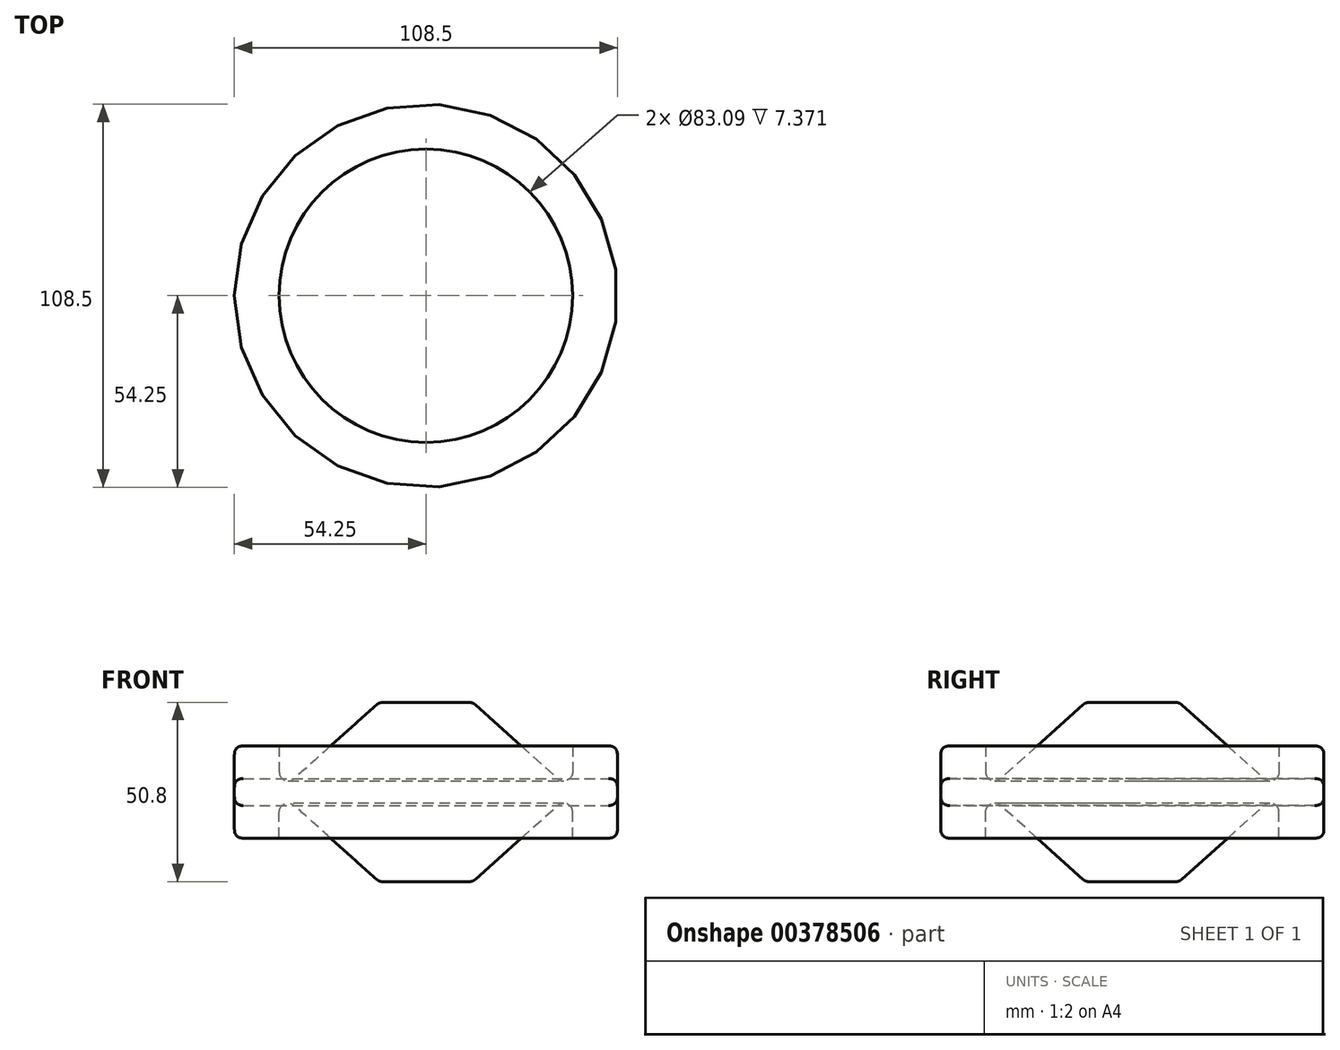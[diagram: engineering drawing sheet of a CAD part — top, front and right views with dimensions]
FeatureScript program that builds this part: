
annotation { "Feature Type Name" : "Feature", "Feature Type Description" : "" }
export const myFeature = defineFeature(function(context is Context, id is Id, definition is map)
    precondition{}
    {
        {
            var Q0;
            Q0=qCreatedBy(makeId("Front.planeOp"),FACE);
            var sketch = newSketch(context, id + "F0", { "sketchPlane" : qUnion([Q0])});
            skLineSegment(sketch, "E0", {"start": v(0, 0) * mm, "end": v(0, 25.4) * mm});
            skLineSegment(sketch, "E1", {"start": v(0, 25.4) * mm, "end": v(-13.24, 25.4) * mm});
            skLineSegment(sketch, "E2", {"start": v(-13.24, 25.4) * mm, "end": v(-41.55, 0) * mm});
            skLineSegment(sketch, "E3", {"start": v(-41.55, 0) * mm, "end": v(-41.55, 13.06) * mm});
            skLineSegment(sketch, "E4", {"start": v(-41.55, 13.06) * mm, "end": v(-54.25, 13.06) * mm});
            skLineSegment(sketch, "E5", {"start": v(-54.25, 13.06) * mm, "end": v(-54.25, 0) * mm});
            skLineSegment(sketch, "E6", {"start": v(-54.25, 0) * mm, "end": v(-54.25, -3.81) * mm});
            skLineSegment(sketch, "E7", {"start": v(-54.25, -3.81) * mm, "end": v(0, -3.81) * mm});
            skLineSegment(sketch, "E8", {"start": v(0, -3.81) * mm, "end": v(0, 0) * mm});
            skSolve(sketch);
        }
        {
            var Q0;
            Q0=makeQuery(id+"F0.imprint","IMPRINT",FACE,{"disambiguationData":[TD([[makeQuery(id+"F0.imprint","IMPRINT",EDGE,{"derivedFrom":sQuery(id+"F0.wireOp",EDGE,"E0")}),1.0]])]});
            var Q1;
            Q1=sQuery(id+"F0.wireOp",EDGE,"E0");
            revolve(context, id + "F1", {"entities" : qUnion([Q0]), "axis" : qUnion([Q1]), "revolveType" : RevolveType.FULL});
        }
        {
            var Q0;
            Q0=makeQuery(id+"F1.opRevolve","SWEPT_FACE",FACE,{"disambiguationData":[OSD([sQuery(id+"F0.wireOp",EDGE,"E2")])]});
            fillet(context, id + "F2", {"entities" : qUnion([Q0]), "radius" : 2.54 * mm, "tangentPropagation" : true, "allowEdgeOverflow" : false});
        }
        {
            var Q0;
            Q0=makeQuery(id+"F1.opRevolve","SWEPT_FACE",FACE,{"disambiguationData":[OSD([sQuery(id+"F0.wireOp",EDGE,"E5"),sQuery(id+"F0.wireOp",EDGE,"E6")])]});
            fillet(context, id + "F3", {"entities" : qUnion([Q0]), "radius" : 2.54 * mm, "tangentPropagation" : true, "rho" : 0.5, "crossSection" : FilletCrossSection.CONIC, "allowEdgeOverflow" : false});
        }
        {
            var Q0;
            Q0=makeQuery(id+"F1.opRevolve","SWEPT_BODY",BODY,{"disambiguationData":[OSD([sQuery(id+"F0.wireOp",EDGE,"E0"),sQuery(id+"F0.wireOp",EDGE,"E1"),sQuery(id+"F0.wireOp",EDGE,"E2"),sQuery(id+"F0.wireOp",EDGE,"E3"),sQuery(id+"F0.wireOp",EDGE,"E4"),sQuery(id+"F0.wireOp",EDGE,"E5"),sQuery(id+"F0.wireOp",EDGE,"E6"),sQuery(id+"F0.wireOp",EDGE,"E7"),sQuery(id+"F0.wireOp",EDGE,"E8")])]});
            var Q1;
            Q1=qCreatedBy(makeId("Top.planeOp"),FACE);
            mirror(context, id + "F4", {"entities" : qUnion([Q0]), "mirrorPlane" : qUnion([Q1])});
        }
    });
